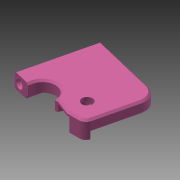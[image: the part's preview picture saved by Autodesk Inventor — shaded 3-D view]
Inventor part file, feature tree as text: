
AUTODESK INVENTOR PART (.ipt)
format: ipt  version: 2014 (Build 180170000, 170)  size: 370,176 bytes
history: native  units: mm
features: sketch x12, extrude x11, other x8, fillet x3, chamfer x3, plane x1, projected_geometry x1
ambient origin geometry x8: Origin, YZ Plane, XZ Plane, XY Plane, X Axis, Y Axis, Z Axis, Center Point
bodies: Solid1 (feature_tree)
feature tree (39):
  sketch  "Sketch1"  dims[d0=7.7mm d1=3.0mm]
  extrude  "Extrusion1"  Depth=3.0mm
  extrude  "Extrusion2"  Depth=1.5mm
  sketch  "Sketch3"  dims[d4=11.0mm d5=11.0mm]
  extrude  "Extrusion3"  Depth=11.0mm
  extrude  "Extrusion4"  Depth=20.0mm
  other  "UCS1"
  extrude  "Extrusion5"  Depth=35.0mm
  extrude  "Extrusion10"  Depth=4.0mm
  extrude  "Extrusion6"  Depth=8.0mm
  extrude  "Extrusion7"  Depth=3.0mm
  fillet  "Fillet2"  Radius=2.0mm
  fillet  "Fillet1"  Radius=5.8mm
  extrude  "Extrusion8"  TaperAngle=0.0deg  [1 undecoded]
  extrude  "Extrusion9"  Depth=9.0mm
  plane  "Work Plane1"
  extrude  "Extrusion11"  Depth=5.0mm
  fillet  "Fillet3"  Radius=1.5mm
  chamfer  "Chamfer1"  Distance=10.0mm
  chamfer  "Chamfer2"  Distance=3.301856mm
  chamfer  "Chamfer3"  Distance=1.0mm
  sketch  "Sketch2"  dims[d2=18.5mm d3=1.5mm]
  sketch  "Sketch4"  dims[d6=26.703538mm d7=20.0mm]
  sketch  "Sketch5"  dims[d8=40.0mm d9=35.0mm]
  sketch  "Sketch6"  dims[d10=4.0mm d11=0.0mm d12=14.0mm]
  projected_geometry  "Projected Loop1"
  sketch  "Sketch7"  dims[d13=19.5mm d14=8.0mm]
  sketch  "Sketch8"  dims[d15=0.0mm d16=0.0mm d17=3.0mm]
  sketch  "Sketch9"  dims[d18=0.0mm d19=0.0mm d20=0.0mm d21=0.0mm d22=0.0mm d23=0.0mm d24=2.0mm d25=0.0mm d26=5.8mm]
  sketch  "Sketch10"  dims[d27=2.0mm d28=0.0mm d29=0.0mm d30=0.0mm]
  sketch  "Sketch11"  dims[d31=9.0mm d32=12.0mm]
  sketch  "Sketch13"  dims[d33=2.0mm d34=0.0mm d35=5.0mm d37=1.5mm d38=0.0mm d39=10.0mm d40=3.301856mm d41=1.0mm d42=8.0mm d43=4.0mm d44=3.0mm d45=11.5mm d46=7.029049mm d47=4.0mm d48=0.0mm d49=3.0mm d50=1.0mm d51=0.5mm d52=2.0mm d53=45.0deg d54=1.0mm d55=2.0mm d56=45.0deg d57=2.5mm d58=0.0mm d59=0.0mm d60=0.0mm d64=-3.5mm d65=3.535mm d66=3.0mm d67=0.0mm d68=0.5mm d69=2.0mm d70=45.0deg]
  other  "UCS1: YZ Plane"
  other  "UCS1: XZ Plane"
  other  "UCS1: XY Plane"
  other  "UCS1: X Axis"
  other  "UCS1: Y Axis"
  other  "UCS1: Z Axis"
  other  "UCS1: Center Point"
note: 1 required parameter value undecoded (feature->parameter linkage not recoverable at this tier; creation-order binding heuristic only, values carry confidence <= 0.55)
